# Revit family: FantiniCosmi_BIM_CH180
name_source: partatom
category: Modelli generici
units: mm (PartAtom-declared; Revit-internal decimal feet)

## family parameters
Basato su piano di lavoro = No
Condiviso = No
Punto di calcolo locali = No
Può ospitare armatura = No
Quota connettore circolare = Usa diametro
Sempre verticale = Sì
Taglio con vuoti quando caricato = No
Tipo di parte = Normale

## types (1)
- Standard
    Adjustable antifreeze temperature range = 0 ÷ 7 °C
    Catalog web link = https://www.fantinicosmi.it
    Connection = 3 screw terminals (contact switching NC and NO)
    Descrizione = Cronotermostato settimanale touchscreen, a batterie
    Displayed temperature = -35 ÷ 50 °C
    Insulation class = II
    Material = ABS Plastic
    Minimum differential = ±0,1K.
    Part Number = Intellicomfort CH180
    Power supply = 2 batteries AA 1,5V
    Preset differential = 0,3 K
    Prospetto di default = 0 mm  [stored 0 ft]
    Protection degree = IP20
    Pulse voltage = 4000V
    Software = A class
    Temperature range = 2 ÷ 40 °C
    Thermal gradient = 4K/h.
    Type of action = 1BU (micro disconnection)

note: [stored X ft] marks values corroborated as IEEE doubles in the binary element streams (Revit-internal decimal feet)

## geometry (parser evidence)
native form markers: Sweep x3
no freeform markers — native parametric forms only
